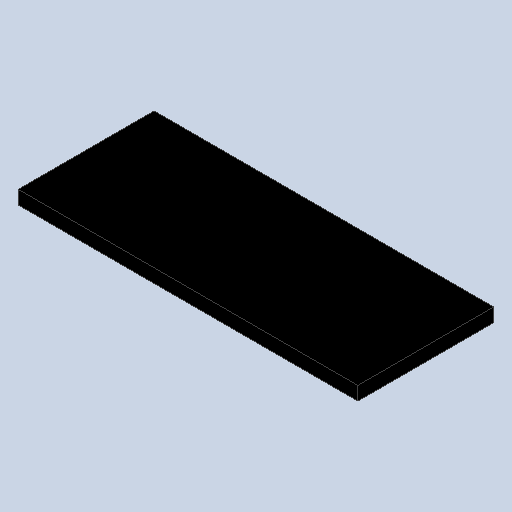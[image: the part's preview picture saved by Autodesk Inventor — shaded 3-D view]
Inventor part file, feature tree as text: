
AUTODESK INVENTOR PART (.ipt)
format: ipt  version: 2025.2 (Build 292293000, 293)  size: 223,744 bytes
history: native  units: mm
features: extrude x1, sketch x1
ambient origin geometry x8: Origin, YZ Plane, XZ Plane, XY Plane, X Axis, Y Axis, Z Axis, Center Point
bodies: Solid1 (feature_tree)
feature tree (2):
  extrude  "Extrusion1"  Depth=10.0mm
  sketch  "Sketch1"  dims[d0=25.0mm d1=10.0mm d2=1.0mm d3=0.0mm]
